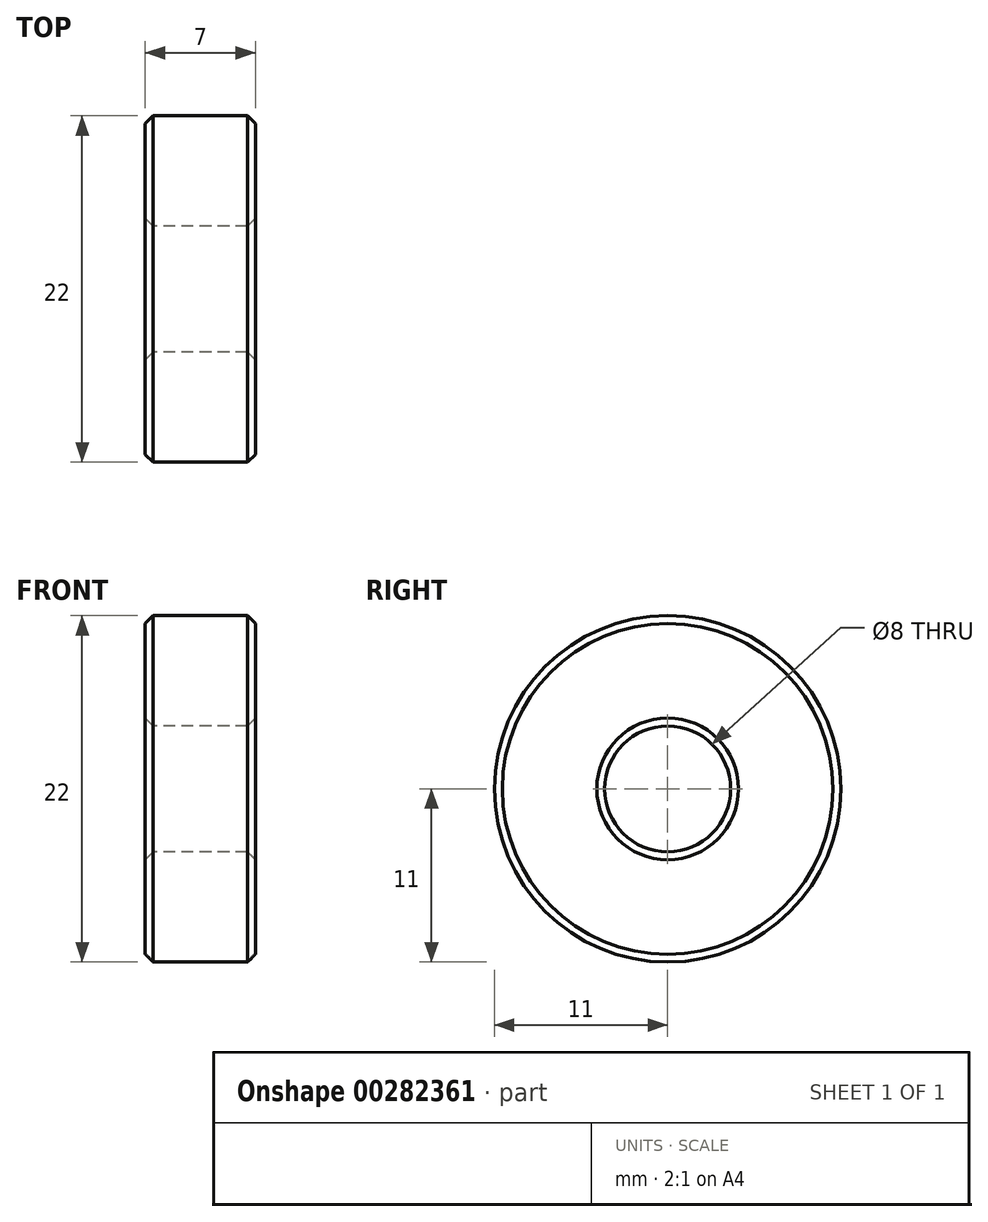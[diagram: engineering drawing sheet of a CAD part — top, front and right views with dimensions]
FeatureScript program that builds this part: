
annotation { "Feature Type Name" : "Feature", "Feature Type Description" : "" }
export const myFeature = defineFeature(function(context is Context, id is Id, definition is map)
    precondition{}
    {
        {
            var Q0;
            Q0=qCreatedBy(makeId("Right.planeOp"),FACE);
            var sketch = newSketch(context, id + "F0", { "sketchPlane" : qUnion([Q0])});
            skCircle(sketch, "E0", {"center": v(0, 0) * mm, "radius": 4 * mm});
            skCircle(sketch, "E1", {"center": v(0, 0) * mm, "radius": 11 * mm});
            skSolve(sketch);
        }
        {
            var Q0;
            Q0=qSketchRegion(id+"F0",true);
            extrude(context, id + "F1", {"entities" : qUnion([Q0]), "depth" : 7 * mm});
        }
        {
            var Q0;
            Q0=makeQuery(id+"F1.opExtrude","CAP_EDGE",EDGE,{"disambiguationData":[OSD([sQuery(id+"F0.wireOp",EDGE,"E1")])],"isStart":false});
            var Q1;
            Q1=makeQuery(id+"F1.opExtrude","CAP_EDGE",EDGE,{"disambiguationData":[OSD([sQuery(id+"F0.wireOp",EDGE,"E0")])],"isStart":false});
            var Q2;
            Q2=makeQuery(id+"F1.opExtrude","CAP_EDGE",EDGE,{"disambiguationData":[OSD([sQuery(id+"F0.wireOp",EDGE,"E1")])],"isStart":true});
            var Q3;
            Q3=makeQuery(id+"F1.opExtrude","CAP_EDGE",EDGE,{"disambiguationData":[OSD([sQuery(id+"F0.wireOp",EDGE,"E0")])],"isStart":true});
            chamfer(context, id + "F2", {"entities" : qUnion([Q0, Q1, Q2, Q3]), "width" : 0.5 * mm, "tangentPropagation" : true});
        }
    });
